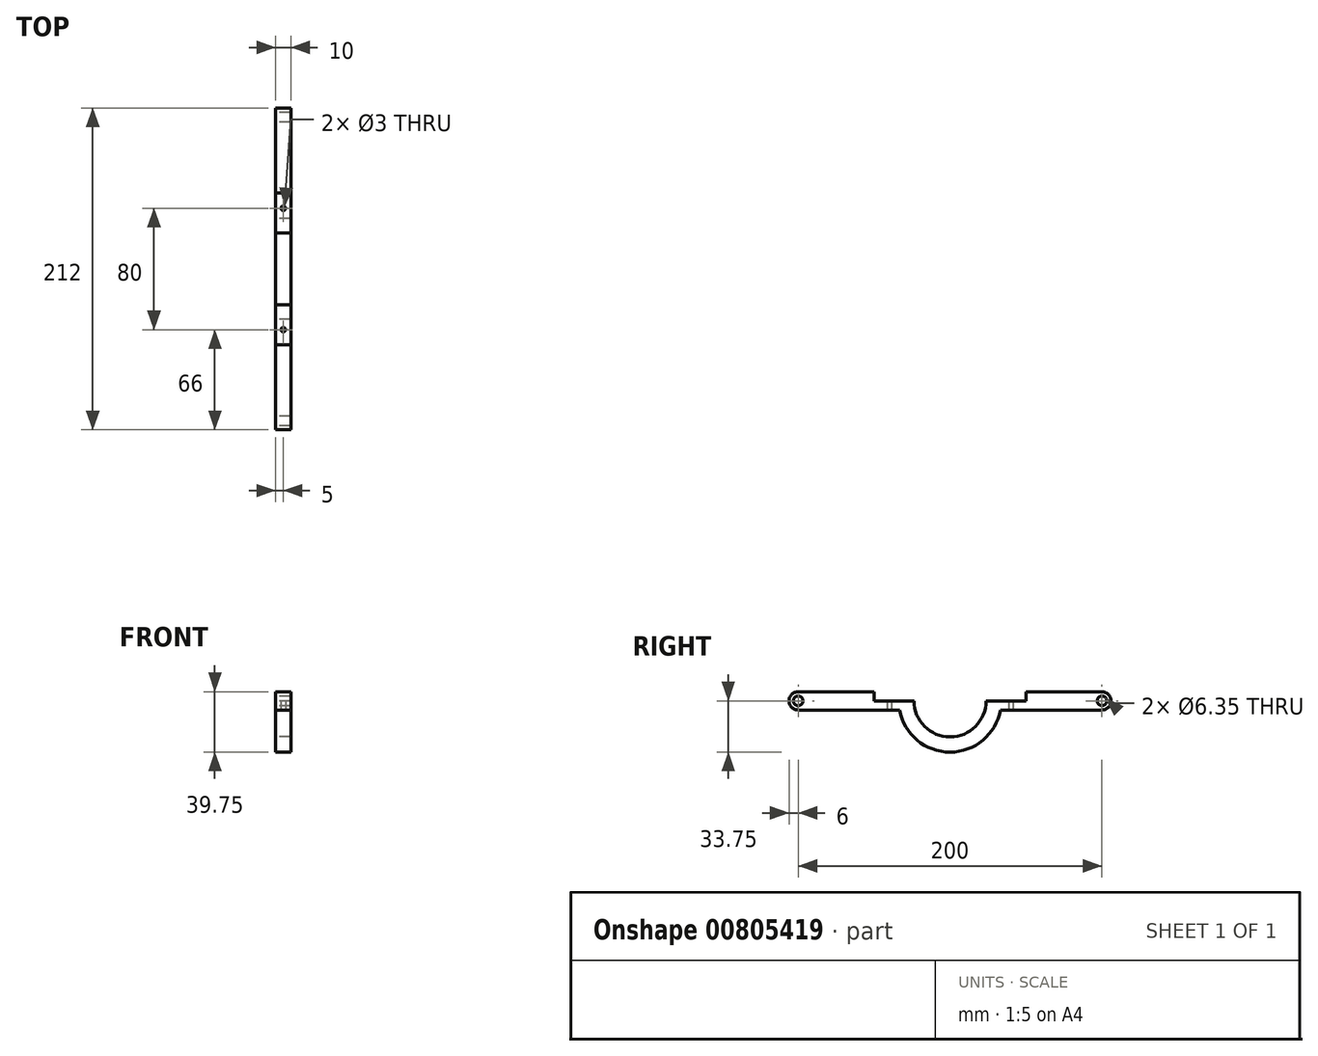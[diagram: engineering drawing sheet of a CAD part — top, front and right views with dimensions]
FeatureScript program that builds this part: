
annotation { "Feature Type Name" : "Feature", "Feature Type Description" : "" }
export const myFeature = defineFeature(function(context is Context, id is Id, definition is map)
    precondition{}
    {
        {
            var Q0;
            Q0=qCreatedBy(makeId("Right.planeOp"),FACE);
            var sketch = newSketch(context, id + "F0", { "sketchPlane" : qUnion([Q0])});
            skArc(sketch, "E0", {"start": v(-23.75, 0) * mm, "mid": v(-16.8, -16.8) * mm, "end": v(0, -23.75) * mm});
            skArc(sketch, "E1", {"start": v(-33.21, -6) * mm, "mid": v(-21.64, -25.9) * mm, "end": v(0, -33.75) * mm});
            skLineSegment(sketch, "E2.bottom", {"start": v(-100, 6) * mm, "end": v(-50, 6) * mm});
            skLineSegment(sketch, "E2.top", {"start": v(-100, -6) * mm, "end": v(-33.21, -6) * mm});
            skPoint(sketch, "E3", {"position": v(-100, 0) * mm});
            skArc(sketch, "E4", {"start": v(-100, -6) * mm, "mid": v(-106, 0) * mm, "end": v(-100, 6) * mm});
            skCircle(sketch, "E5", {"center": v(-100, 0) * mm, "radius": 3.17 * mm});
            skLineSegment(sketch, "E6.top", {"start": v(-50, 0) * mm, "end": v(-23.75, 0) * mm});
            skLineSegment(sketch, "E6.left", {"start": v(-50, 6) * mm, "end": v(-50, 0) * mm});
            skCircle(sketch, "E7.MirrorC", {"center": v(100, 0) * mm, "radius": 3.17 * mm});
            skLineSegment(sketch, "E8.MirrorCS", {"start": v(50, 0) * mm, "end": v(23.75, 0) * mm});
            skArc(sketch, "E9.MirrorCS", {"start": v(23.75, 0) * mm, "mid": v(16.8, -16.8) * mm, "end": v(0, -23.75) * mm});
            skLineSegment(sketch, "E10.MirrorCS", {"start": v(100, -6) * mm, "end": v(33.21, -6) * mm});
            skLineSegment(sketch, "E11.MirrorCS", {"start": v(50, 6) * mm, "end": v(50, 0) * mm});
            skArc(sketch, "E12.MirrorCS", {"start": v(100, -6) * mm, "mid": v(106, 0) * mm, "end": v(100, 6) * mm});
            skLineSegment(sketch, "E13.MirrorCS", {"start": v(100, 6) * mm, "end": v(50, 6) * mm});
            skArc(sketch, "E14.MirrorCS", {"start": v(33.21, -6) * mm, "mid": v(21.64, -25.9) * mm, "end": v(0, -33.75) * mm});
            skLineSegment(sketch, "E15", {"start": v(0, -23.75) * mm, "end": v(0, -33.75) * mm, "construction": true});
            skSolve(sketch);
        }
        {
            var Q0;
            Q0 = qSketchRegion(id + "F0", true);
            extrude(context, id + "F1", {"entities" : qUnion([Q0]), "depth" : 10 * mm, "offsetDistance" : 25 * mm});
        }
        {
            var Q0;
            Q0=makeQuery(id+"F1.opExtrude","SWEPT_FACE",FACE,{"disambiguationData":[OSD([sQuery(id+"F0.wireOp",EDGE,"E2.top")])]});
            var sketch = newSketch(context, id + "F2", { "sketchPlane" : qUnion([Q0])});
            skLineSegment(sketch, "E16.0", {"start": v(0, 100) * mm, "end": v(0, 33.21) * mm, "construction": true});
            skLineSegment(sketch, "E17.0", {"start": v(10, 100) * mm, "end": v(10, 33.21) * mm, "construction": true});
            skPoint(sketch, "E18.0", {"position": v(5, 100) * mm});
            skPoint(sketch, "E19.0", {"position": v(5, 33.21) * mm});
            skLineSegment(sketch, "E20", {"start": v(5, 100) * mm, "end": v(5, 33.21) * mm, "construction": true});
            skCircle(sketch, "E21", {"center": v(5, 40) * mm, "radius": 1.5 * mm});
            skCircle(sketch, "E22.MirrorC", {"center": v(5, -40) * mm, "radius": 1.5 * mm});
            skLineSegment(sketch, "E23.MirrorCS", {"start": v(5, -100) * mm, "end": v(5, -33.21) * mm, "construction": true});
            skSolve(sketch);
        }
        {
            var Q0;
            Q0 = qSketchRegion(id + "F2", true);
            extrude(context, id + "F3", {"entities" : qUnion([Q0]), "operationType" : NewBodyOperationType.REMOVE, "oppositeDirection" : true, "depth" : 25 * mm, "offsetDistance" : 25 * mm});
        }
    });
